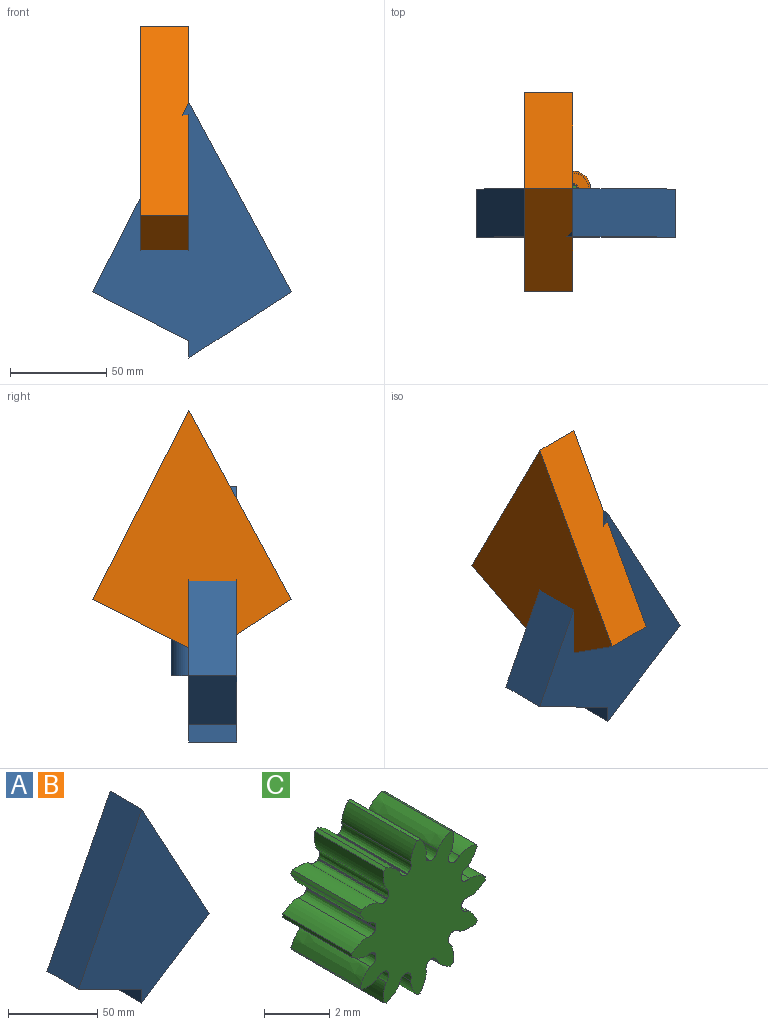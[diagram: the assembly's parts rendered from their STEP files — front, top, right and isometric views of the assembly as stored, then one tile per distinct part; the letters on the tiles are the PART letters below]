
ASSEMBLY  parts=3 mates=4
PART A: 12 faces, bbox 103.4x34.3x132.8 mm
  f0: cylinder r=9.25mm len=40mm, axis (0,0,-1), area 1162.4mm2, adj f1,f2,f5
  f1: plane 18.5x9.25mm, normal (0,0,1), area 27.5mm2, adj f0,f3,f5
  f2: plane 18.5x9.25mm, normal (0,0,-1), area 134.4mm2, adj f0,f5
  f3: cylinder r=8.25mm len=39mm, axis (0,0,-1), area 1010.8mm2, adj f1,f4,f5
  f4: plane 16.5x8.25mm, normal (0,0,1), area 106.9mm2, adj f3,f5
  f5: plane 132.8x103.36mm, normal (0,1,0), area 6542.6mm2, adj f0,f1,f2,f3,f4,f6,f7,f8
  f6: plane 98.39x53.3mm, normal (0.88,0,0.48), area 2797.4mm2, adj f5,f7,f10,f11
  f7: plane 98.39x50.06mm, normal (-0.89,0,0.45), area 2759.8mm2, adj f5,f6,f8,f11
  f8: plane 50.06x25.47mm, normal (-0.45,0,-0.89), area 1404.2mm2, adj f5,f7,f9,f11
  f9: plane 25x8.94mm, normal (-1,0,0), area 223.5mm2, adj f5,f8,f10,f11
  f10: plane 53.3x34.41mm, normal (0.54,0,-0.84), area 1586mm2, adj f5,f6,f9,f11
  f11: plane 132.8x103.36mm, normal (0,-1,0), area 6639.1mm2, adj f6,f7,f8,f9,f10
PART B: same geometry as A
PART C: 86 faces, bbox 5.8x3x5.8 mm
  f0: cylinder r=2.9mm len=3mm, axis (0,1,0), area 0.4mm2, adj f3,f4,f32,f43
  f1: cylinder r=2.9mm len=3mm, axis (0,1,0), area 0.4mm2, adj f3,f4,f19,f80
  f2: cylinder r=2.9mm len=3mm, axis (0,1,0), area 0.4mm2, adj f3,f4,f74,f85
  f3: plane 5.79x5.79mm, normal (0,-1,0), area 18.2mm2, adj f0,f1,f2,f5,f6,f7,f8,f9
  f4: plane 5.79x5.79mm, normal (0,1,0), area 18.2mm2, adj f0,f1,f2,f5,f6,f7,f8,f9
  f5: cylinder r=2.9mm len=3mm, axis (0,1,0), area 0.4mm2, adj f3,f4,f68,f79
  f6: cylinder r=2.9mm len=3mm, axis (0,1,0), area 0.4mm2, adj f3,f4,f62,f73
  f7: cylinder r=2.9mm len=3mm, axis (0,1,0), area 0.4mm2, adj f3,f4,f56,f67
  f8: cylinder r=2.9mm len=3mm, axis (0,1,0), area 0.4mm2, adj f3,f4,f50,f61
  f9: cylinder r=2.9mm len=3mm, axis (0,1,0), area 0.4mm2, adj f3,f4,f44,f55
  f10: cylinder r=2.9mm len=3mm, axis (0,1,0), area 0.4mm2, adj f3,f4,f38,f49
  f11: cylinder r=2.9mm len=3mm, axis (0,1,0), area 0.4mm2, adj f3,f4,f26,f37
  f12: cylinder r=2.9mm len=3mm, axis (0,1,0), area 0.4mm2, adj f3,f4,f20,f31
  f13: cylinder r=2.9mm len=3mm, axis (0,1,0), area 0.4mm2, adj f3,f4,f14,f25
  f14: extruded ~3x0.66mm, area 2.2mm2, adj f3,f4,f13,f15
  f15: extruded ~3x0.36mm, area 1.3mm2, adj f3,f4,f14,f16
  f16: cylinder r=1.93mm len=3mm, axis (0,1,0), area 0.1mm2, adj f3,f4,f15,f17
  f17: cylinder r=1.93mm len=3mm, axis (0,1,0), area 0.1mm2, adj f3,f4,f16,f18
  f18: extruded ~3x0.3mm, area 1.3mm2, adj f3,f4,f17,f19
  f19: extruded ~3x0.57mm, area 2.2mm2, adj f1,f3,f4,f18
  f20: extruded ~3x0.57mm, area 2.2mm2, adj f3,f4,f12,f21
  f21: extruded ~3x0.3mm, area 1.3mm2, adj f3,f4,f20,f22
  f22: cylinder r=1.93mm len=3mm, axis (0,1,0), area 0.1mm2, adj f3,f4,f21,f23
  f23: cylinder r=1.93mm len=3mm, axis (0,1,0), area 0.1mm2, adj f3,f4,f22,f24
  f24: extruded ~3x0.36mm, area 1.3mm2, adj f3,f4,f23,f25
  f25: extruded ~3x0.66mm, area 2.2mm2, adj f3,f4,f13,f24
  f26: extruded ~3x0.71mm, area 2.2mm2, adj f3,f4,f11,f27
  f27: extruded ~3x0.39mm, area 1.3mm2, adj f3,f4,f26,f28
  f28: cylinder r=1.93mm len=3mm, axis (0,1,0), area 0.1mm2, adj f3,f4,f27,f29
  f29: cylinder r=1.93mm len=3mm, axis (0,1,0), area 0.1mm2, adj f3,f4,f28,f30
  f30: extruded ~3x0.39mm, area 1.3mm2, adj f3,f4,f29,f31
  f31: extruded ~3x0.71mm, area 2.2mm2, adj f3,f4,f12,f30
  f32: extruded ~3x0.66mm, area 2.2mm2, adj f0,f3,f4,f33
  f33: extruded ~3x0.36mm, area 1.3mm2, adj f3,f4,f32,f34
  f34: cylinder r=1.93mm len=3mm, axis (0,1,0), area 0.1mm2, adj f3,f4,f33,f35
  f35: cylinder r=1.93mm len=3mm, axis (0,1,0), area 0.1mm2, adj f3,f4,f34,f36
  f36: extruded ~3x0.3mm, area 1.3mm2, adj f3,f4,f35,f37
  f37: extruded ~3x0.57mm, area 2.2mm2, adj f3,f4,f11,f36
  f38: extruded ~3x0.57mm, area 2.2mm2, adj f3,f4,f10,f39
  f39: extruded ~3x0.3mm, area 1.3mm2, adj f3,f4,f38,f40
  f40: cylinder r=1.93mm len=3mm, axis (0,1,0), area 0.1mm2, adj f3,f4,f39,f41
  f41: cylinder r=1.93mm len=3mm, axis (0,1,0), area 0.1mm2, adj f3,f4,f40,f42
  f42: extruded ~3x0.36mm, area 1.3mm2, adj f3,f4,f41,f43
  f43: extruded ~3x0.66mm, area 2.2mm2, adj f0,f3,f4,f42
  f44: extruded ~3x0.71mm, area 2.2mm2, adj f3,f4,f9,f45
  f45: extruded ~3x0.39mm, area 1.3mm2, adj f3,f4,f44,f46
  f46: cylinder r=1.93mm len=3mm, axis (0,1,0), area 0.1mm2, adj f3,f4,f45,f47
  f47: cylinder r=1.93mm len=3mm, axis (0,1,0), area 0.1mm2, adj f3,f4,f46,f48
  f48: extruded ~3x0.39mm, area 1.3mm2, adj f3,f4,f47,f49
  f49: extruded ~3x0.71mm, area 2.2mm2, adj f3,f4,f10,f48
  f50: extruded ~3x0.66mm, area 2.2mm2, adj f3,f4,f8,f51
  f51: extruded ~3x0.36mm, area 1.3mm2, adj f3,f4,f50,f52
  f52: cylinder r=1.93mm len=3mm, axis (0,1,0), area 0.1mm2, adj f3,f4,f51,f53
  f53: cylinder r=1.93mm len=3mm, axis (0,1,0), area 0.1mm2, adj f3,f4,f52,f54
  f54: extruded ~3x0.3mm, area 1.3mm2, adj f3,f4,f53,f55
  f55: extruded ~3x0.57mm, area 2.2mm2, adj f3,f4,f9,f54
  f56: extruded ~3x0.57mm, area 2.2mm2, adj f3,f4,f7,f57
  f57: extruded ~3x0.3mm, area 1.3mm2, adj f3,f4,f56,f58
  f58: cylinder r=1.93mm len=3mm, axis (0,1,0), area 0.1mm2, adj f3,f4,f57,f59
  f59: cylinder r=1.93mm len=3mm, axis (0,1,0), area 0.1mm2, adj f3,f4,f58,f60
  f60: extruded ~3x0.36mm, area 1.3mm2, adj f3,f4,f59,f61
  f61: extruded ~3x0.66mm, area 2.2mm2, adj f3,f4,f8,f60
  f62: extruded ~3x0.71mm, area 2.2mm2, adj f3,f4,f6,f63
  f63: extruded ~3x0.39mm, area 1.3mm2, adj f3,f4,f62,f64
  f64: cylinder r=1.93mm len=3mm, axis (0,1,0), area 0.1mm2, adj f3,f4,f63,f65
  f65: cylinder r=1.93mm len=3mm, axis (0,1,0), area 0.1mm2, adj f3,f4,f64,f66
  f66: extruded ~3x0.39mm, area 1.3mm2, adj f3,f4,f65,f67
  f67: extruded ~3x0.71mm, area 2.2mm2, adj f3,f4,f7,f66
  f68: extruded ~3x0.66mm, area 2.2mm2, adj f3,f4,f5,f69
  f69: extruded ~3x0.36mm, area 1.3mm2, adj f3,f4,f68,f70
  f70: cylinder r=1.93mm len=3mm, axis (0,1,0), area 0.1mm2, adj f3,f4,f69,f71
  f71: cylinder r=1.93mm len=3mm, axis (0,1,0), area 0.1mm2, adj f3,f4,f70,f72
  f72: extruded ~3x0.3mm, area 1.3mm2, adj f3,f4,f71,f73
  f73: extruded ~3x0.57mm, area 2.2mm2, adj f3,f4,f6,f72
  f74: extruded ~3x0.57mm, area 2.2mm2, adj f2,f3,f4,f75
  f75: extruded ~3x0.3mm, area 1.3mm2, adj f3,f4,f74,f76
  f76: cylinder r=1.93mm len=3mm, axis (0,1,0), area 0.1mm2, adj f3,f4,f75,f77
  f77: cylinder r=1.93mm len=3mm, axis (0,1,0), area 0.1mm2, adj f3,f4,f76,f78
  f78: extruded ~3x0.36mm, area 1.3mm2, adj f3,f4,f77,f79
  f79: extruded ~3x0.66mm, area 2.2mm2, adj f3,f4,f5,f78
  f80: extruded ~3x0.71mm, area 2.2mm2, adj f1,f3,f4,f81
  f81: extruded ~3x0.39mm, area 1.3mm2, adj f3,f4,f80,f82
  f82: cylinder r=1.93mm len=3mm, axis (0,1,0), area 0.1mm2, adj f3,f4,f81,f83
  f83: cylinder r=1.93mm len=3mm, axis (0,1,0), area 0.1mm2, adj f3,f4,f82,f84
  f84: extruded ~3x0.39mm, area 1.3mm2, adj f3,f4,f83,f85
  f85: extruded ~3x0.71mm, area 2.2mm2, adj f2,f3,f4,f84
PLACE A t=(-62.81,6.13,-26.06)mm fixed
PLACE B rot(axis=(0,0,-1),90deg) t=(-62.81,6.13,13.94)mm
PLACE C rot(axis=(0.08,-0.7,-0.7),170.9deg) t=(-62.81,6.13,52.44)mm
MATE fastened A.f1 <-> B.f0  axis (0,0,1) through (-62.81,11.7,13.94)mm
MATE cylindrical A.f0 <-> B.f0  axis (0,0,-1) through (-62.81,6.13,-6.06)mm
MATE cylindrical C.f0 <-> B.f0  axis (0,0,-1) through (-62.81,6.13,50.94)mm
MATE planar C.f0 <-> B.f1  axis (0,0,1) through (-62.81,6.13,53.94)mm
